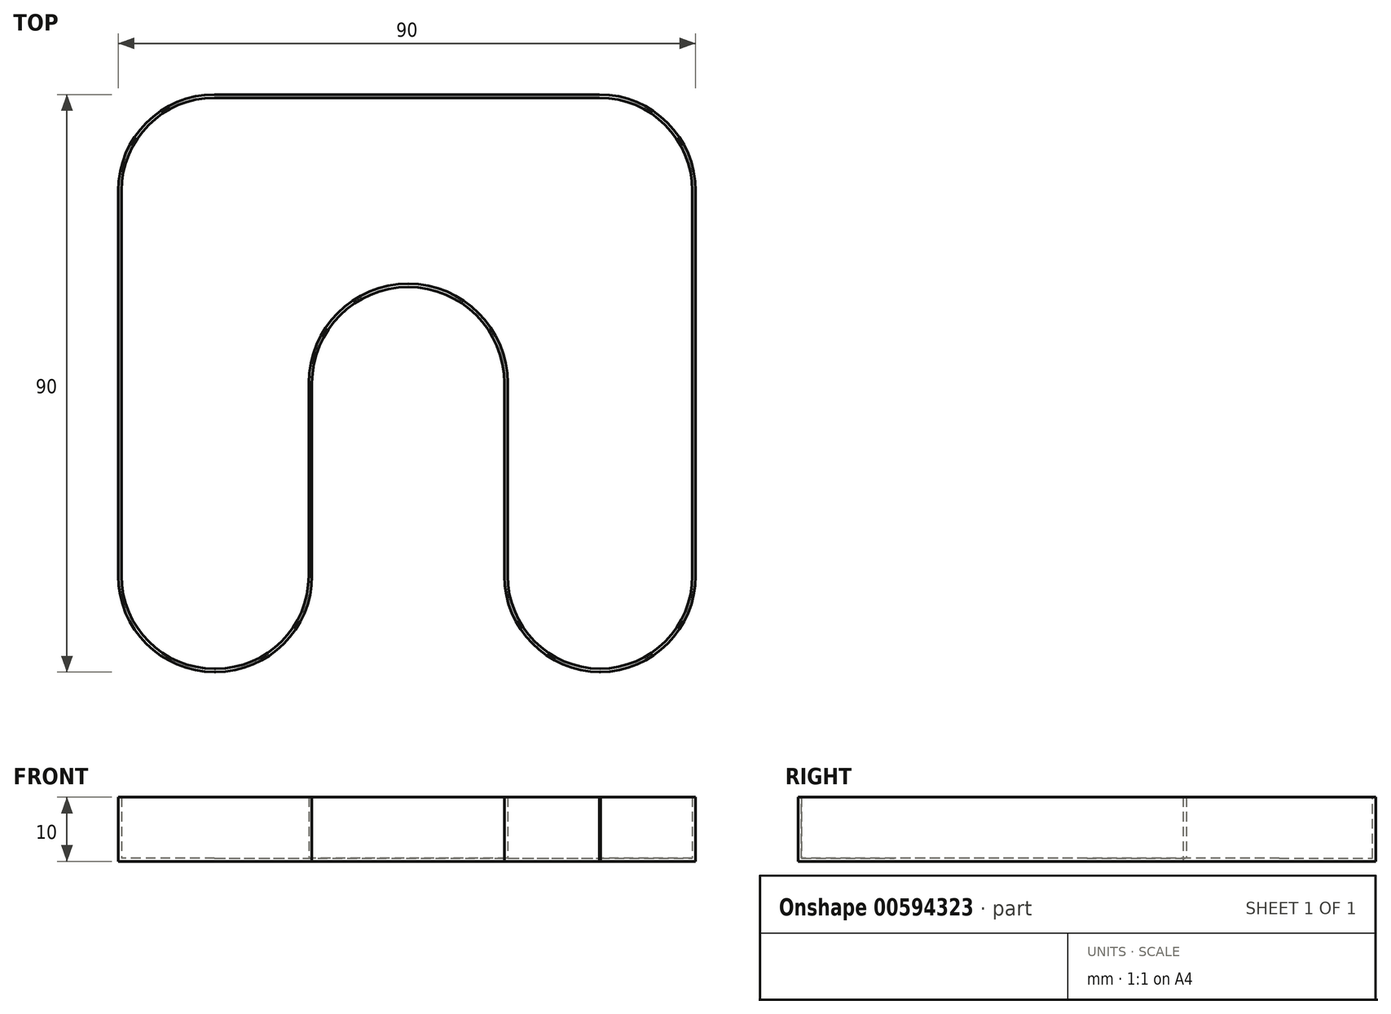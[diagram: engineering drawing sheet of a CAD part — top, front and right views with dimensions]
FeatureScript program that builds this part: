
annotation { "Feature Type Name" : "Feature", "Feature Type Description" : "" }
export const myFeature = defineFeature(function(context is Context, id is Id, definition is map)
    precondition{}
    {
        {
            var Q0;
            Q0=qCreatedBy(makeId("Top.planeOp"),FACE);
            var sketch = newSketch(context, id + "F0", { "sketchPlane" : qUnion([Q0])});
            skLineSegment(sketch, "E0.bottom", {"start": v(-30.06, 44.56) * mm, "end": v(29.94, 44.56) * mm});
            skLineSegment(sketch, "E0.top", {"start": v(-30.06, -45.44) * mm, "end": v(-29.86, -45.44) * mm});
            skLineSegment(sketch, "E0.left", {"start": v(-45.06, 29.56) * mm, "end": v(-45.06, -30.44) * mm});
            skLineSegment(sketch, "E0.right", {"start": v(44.94, 29.56) * mm, "end": v(44.94, -30.44) * mm});
            skLineSegment(sketch, "E1.bottom", {"start": v(0.14, 14.56) * mm, "end": v(0.14, 14.56) * mm});
            skLineSegment(sketch, "E1.top", {"start": v(-14.86, -45.44) * mm, "end": v(15.14, -45.44) * mm});
            skLineSegment(sketch, "E1.left", {"start": v(-14.86, -0.44) * mm, "end": v(-14.86, -30.44) * mm});
            skLineSegment(sketch, "E1.right", {"start": v(15.14, -0.44) * mm, "end": v(15.14, -30.44) * mm});
            skPoint(sketch, "E2.visualSharp", {"position": v(-45.06, 44.56) * mm});
            skArc(sketch, "E2.filletArc", {"start": v(-30.06, 44.56) * mm, "mid": v(-40.66, 40.17) * mm, "end": v(-45.06, 29.56) * mm});
            skPoint(sketch, "E3.visualSharp", {"position": v(44.94, 44.56) * mm});
            skArc(sketch, "E3.filletArc", {"start": v(44.94, 29.56) * mm, "mid": v(40.55, 40.17) * mm, "end": v(29.94, 44.56) * mm});
            skPoint(sketch, "E4.visualSharp", {"position": v(-45.06, -45.44) * mm});
            skArc(sketch, "E4.filletArc", {"start": v(-45.06, -30.44) * mm, "mid": v(-40.66, -41.04) * mm, "end": v(-30.06, -45.44) * mm});
            skArc(sketch, "E5.filletArc", {"start": v(-29.86, -45.44) * mm, "mid": v(-19.25, -41.04) * mm, "end": v(-14.86, -30.44) * mm});
            skPoint(sketch, "E6.visualSharp", {"position": v(-14.86, 14.56) * mm});
            skArc(sketch, "E6.filletArc", {"start": v(0.14, 14.56) * mm, "mid": v(-10.47, 10.17) * mm, "end": v(-14.86, -0.44) * mm});
            skPoint(sketch, "E7.visualSharp", {"position": v(15.14, 14.56) * mm});
            skArc(sketch, "E7.filletArc", {"start": v(15.14, -0.44) * mm, "mid": v(10.75, 10.17) * mm, "end": v(0.14, 14.56) * mm});
            skLineSegment(sketch, "E8", {"start": v(29.94, -45.44) * mm, "end": v(30.14, -45.44) * mm});
            skPoint(sketch, "E9.visualSharp", {"position": v(15.14, -45.44) * mm});
            skArc(sketch, "E9.filletArc", {"start": v(15.14, -30.44) * mm, "mid": v(19.53, -41.04) * mm, "end": v(30.14, -45.44) * mm});
            skPoint(sketch, "E10.visualSharp", {"position": v(44.94, -45.44) * mm});
            skArc(sketch, "E10.filletArc", {"start": v(29.94, -45.44) * mm, "mid": v(40.55, -41.04) * mm, "end": v(44.94, -30.44) * mm});
            skSolve(sketch);
        }
        {
            var Q0;
            Q0 = qSketchRegion(id + "F0", true);
            extrude(context, id + "F1", {"entities" : qUnion([Q0]), "depth" : 10 * mm, "offsetDistance" : 25 * mm});
        }
        {
            var Q0;
            Q0=makeQuery(id+"F1.opExtrude","CAP_FACE",FACE,{"disambiguationData":[OSD([sQuery(id+"F0.wireOp",EDGE,"E0.bottom"),sQuery(id+"F0.wireOp",EDGE,"E0.top"),sQuery(id+"F0.wireOp",EDGE,"E0.left"),sQuery(id+"F0.wireOp",EDGE,"E0.right"),sQuery(id+"F0.wireOp",EDGE,"E1.left"),sQuery(id+"F0.wireOp",EDGE,"E1.right"),sQuery(id+"F0.wireOp",EDGE,"E2.filletArc"),sQuery(id+"F0.wireOp",EDGE,"E3.filletArc"),sQuery(id+"F0.wireOp",EDGE,"E4.filletArc"),sQuery(id+"F0.wireOp",EDGE,"E5.filletArc"),sQuery(id+"F0.wireOp",EDGE,"E6.filletArc"),sQuery(id+"F0.wireOp",EDGE,"E7.filletArc"),sQuery(id+"F0.wireOp",EDGE,"E9.filletArc"),sQuery(id+"F0.wireOp",EDGE,"E10.filletArc")])],"isStart":false});
            shell(context, id + "F2", {"entities" : qUnion([Q0]), "thickness" : 0.5 * mm});
        }
    });
